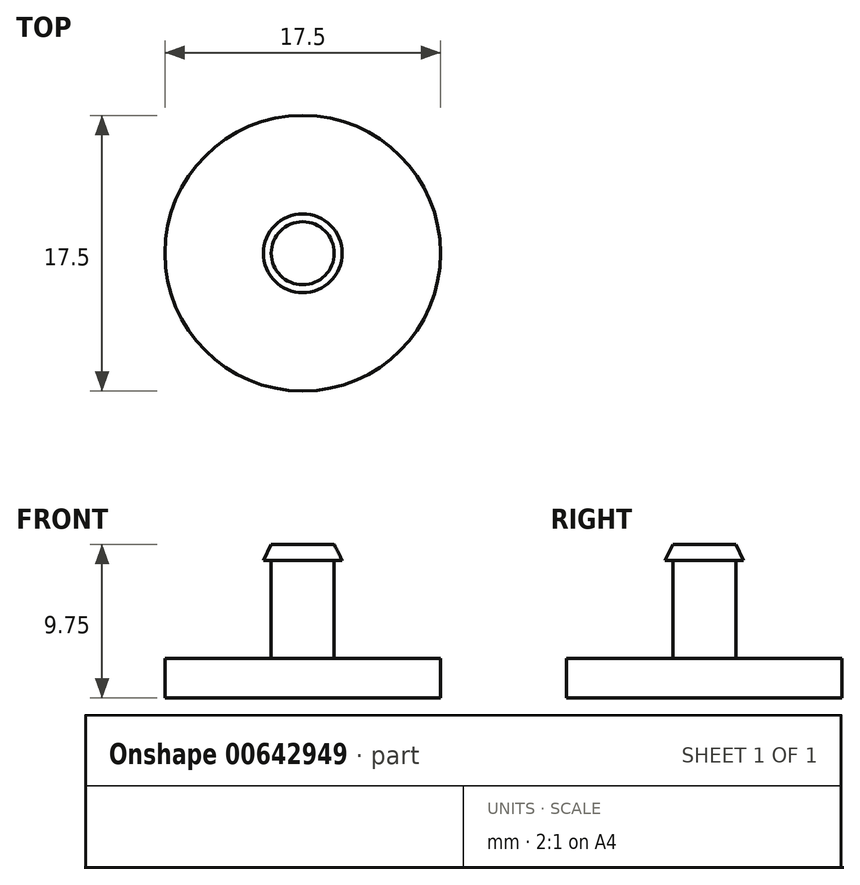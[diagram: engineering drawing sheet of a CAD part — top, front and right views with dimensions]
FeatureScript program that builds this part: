
annotation { "Feature Type Name" : "Feature", "Feature Type Description" : "" }
export const myFeature = defineFeature(function(context is Context, id is Id, definition is map)
    precondition{}
    {
        {
            var Q0;
            Q0=qCreatedBy(makeId("Top.planeOp"),FACE);
            var sketch = newSketch(context, id + "F0", { "sketchPlane" : qUnion([Q0])});
            skCircle(sketch, "E0", {"center": v(0, 0) * mm, "radius": 8.75 * mm});
            skSolve(sketch);
        }
        {
            var Q0;
            Q0=makeQuery(id+"F0.imprint","IMPRINT",FACE,{"disambiguationData":[TD([[makeQuery(id+"F0.imprint","IMPRINT",EDGE,{"derivedFrom":sQuery(id+"F0.wireOp",EDGE,"E0")}),1.0]])]});
            extrude(context, id + "F1", {"entities" : qUnion([Q0]), "depth" : 2.5 * mm, "offsetDistance" : 25.4 * mm});
        }
        {
            var Q0;
            Q0=makeQuery(id+"F1.opExtrude","CAP_FACE",FACE,{"disambiguationData":[OSD([sQuery(id+"F0.wireOp",EDGE,"E0")])],"isStart":false});
            var sketch = newSketch(context, id + "F2", { "sketchPlane" : qUnion([Q0])});
            skCircle(sketch, "E1", {"center": v(0, 0) * mm, "radius": 2 * mm});
            skSolve(sketch);
        }
        {
            var Q0;
            Q0=makeQuery(id+"F2.imprint","IMPRINT",FACE,{"disambiguationData":[TD([[makeQuery(id+"F2.imprint","IMPRINT",EDGE,{"derivedFrom":sQuery(id+"F2.wireOp",EDGE,"E1")}),1.0]])]});
            extrude(context, id + "F3", {"entities" : qUnion([Q0]), "operationType" : NewBodyOperationType.ADD, "depth" : 6.25 * mm, "offsetDistance" : 25.4 * mm});
        }
        {
            var Q0;
            Q0=makeQuery(id+"F3.opExtrude","CAP_FACE",FACE,{"disambiguationData":[OSD([sQuery(id+"F2.wireOp",EDGE,"E1")])],"isStart":false});
            var sketch = newSketch(context, id + "F4", { "sketchPlane" : qUnion([Q0])});
            skCircle(sketch, "E2", {"center": v(0, 0) * mm, "radius": 2.5 * mm});
            skSolve(sketch);
        }
        {
            var Q0;
            Q0=makeQuery(id+"F4.imprint","IMPRINT",FACE,{"disambiguationData":[TD([[makeQuery(id+"F4.imprint","IMPRINT",EDGE,{"derivedFrom":makeQuery(id+"F3.opExtrude","CAP_EDGE",EDGE,{"disambiguationData":[OSD([sQuery(id+"F2.wireOp",EDGE,"E1")])],"isStart":false})}),1.0]])]});
            cPlane(context, id + "F5", {"entities" : qUnion([Q0]), "cplaneType" : CPlaneType.OFFSET, "offset" : 1 * mm, "width" : 152.4 * mm, "height" : 152.4 * mm});
        }
        {
            var Q0;
            Q0=qCreatedBy(id+"F5.planeOp",FACE);
            var sketch = newSketch(context, id + "F6", { "sketchPlane" : qUnion([Q0])});
            skCircle(sketch, "E3", {"center": v(0, 0) * mm, "radius": 2 * mm});
            skSolve(sketch);
        }
        {
            var Q1;
            Q1 = qSketchRegion(id + "F4", true);
            var Q2;
            Q2 = qSketchRegion(id + "F6", true);
            loft(context, id + "F7", {"operationType" : NewBodyOperationType.ADD, "sheetProfilesArray" : [{ "sheetProfileEntities" : qUnion([Q1]) }, { "sheetProfileEntities" : qUnion([Q2]) }]});
        }
    });
